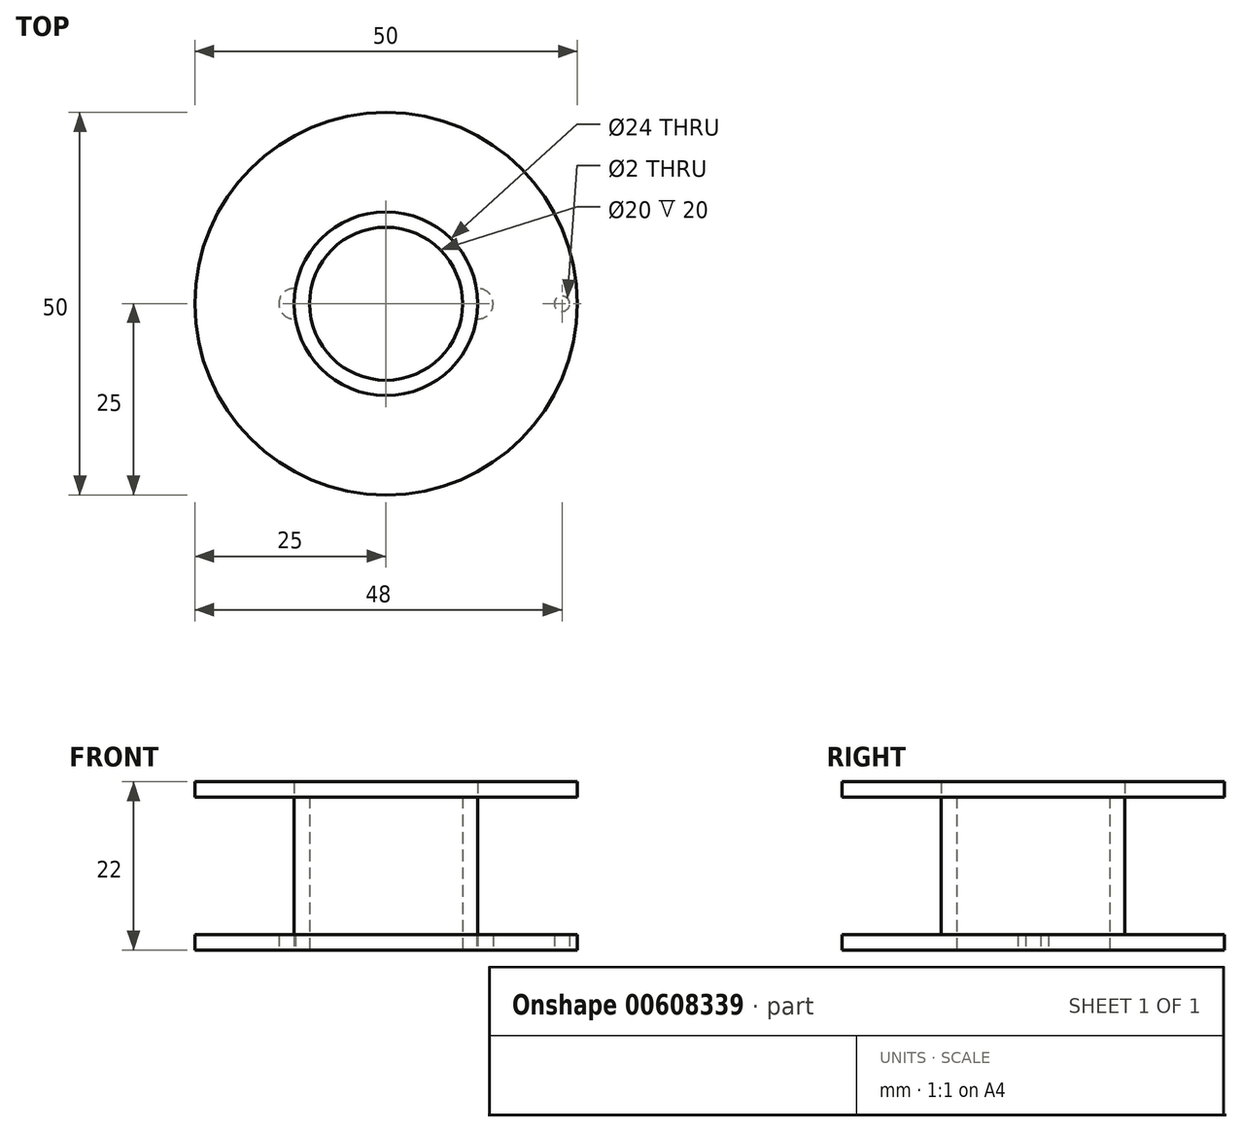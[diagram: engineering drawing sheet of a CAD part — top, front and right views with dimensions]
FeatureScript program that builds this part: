
annotation { "Feature Type Name" : "Feature", "Feature Type Description" : "" }
export const myFeature = defineFeature(function(context is Context, id is Id, definition is map)
    precondition{}
    {
        {
            var Q0;
            Q0=qCreatedBy(makeId("Top.planeOp"),FACE);
            var sketch = newSketch(context, id + "F0", { "sketchPlane" : qUnion([Q0])});
            skCircle(sketch, "E0", {"center": v(0, 0) * mm, "radius": 25 * mm});
            skCircle(sketch, "E1", {"center": v(0, 0) * mm, "radius": 10 * mm});
            skCircle(sketch, "E2", {"center": v(0, 0) * mm, "radius": 12 * mm});
            skArc(sketch, "E3", {"start": v(11.83, -2) * mm, "mid": v(14, 0) * mm, "end": v(11.83, 2) * mm});
            skArc(sketch, "E4", {"start": v(-11.83, 2) * mm, "mid": v(-14, 0) * mm, "end": v(-11.83, -2) * mm});
            skCircle(sketch, "E5", {"center": v(23, 0) * mm, "radius": 1 * mm});
            skSolve(sketch);
        }
        {
            var Q0;
            Q0 = qSketchRegion(id + "F0", true);
            extrude(context, id + "F1", {"entities" : qUnion([Q0]), "depth" : 2 * mm, "offsetDistance" : 25 * mm});
        }
        {
            var Q0;
            Q0=makeQuery(id+"F0.imprint","IMPRINT",FACE,{"disambiguationData":[TD([[makeQuery(id+"F0.imprint","IMPRINT",EDGE,{"derivedFrom":sQuery(id+"F0.wireOp",EDGE,"E1")}),-1.0]])]});
            extrude(context, id + "F2", {"entities" : qUnion([Q0]), "operationType" : NewBodyOperationType.ADD, "depth" : 20 * mm, "offsetDistance" : 25 * mm});
        }
        {
            var Q0;
            Q0=makeQuery(id+"F2.opExtrude","CAP_FACE",FACE,{"disambiguationData":[OSD([sQuery(id+"F0.wireOp",EDGE,"E1"),sQuery(id+"F0.wireOp",EDGE,"E2")])],"isStart":false});
            var sketch = newSketch(context, id + "F3", { "sketchPlane" : qUnion([Q0])});
            skCircle(sketch, "E6", {"center": v(0, 0) * mm, "radius": 25 * mm});
            skCircle(sketch, "E7", {"center": v(0, 0) * mm, "radius": 12 * mm});
            skSolve(sketch);
        }
        {
            var Q0;
            Q0 = qSketchRegion(id + "F3", true);
            extrude(context, id + "F4", {"entities" : qUnion([Q0]), "depth" : 2 * mm, "offsetDistance" : 25 * mm});
        }
    });
